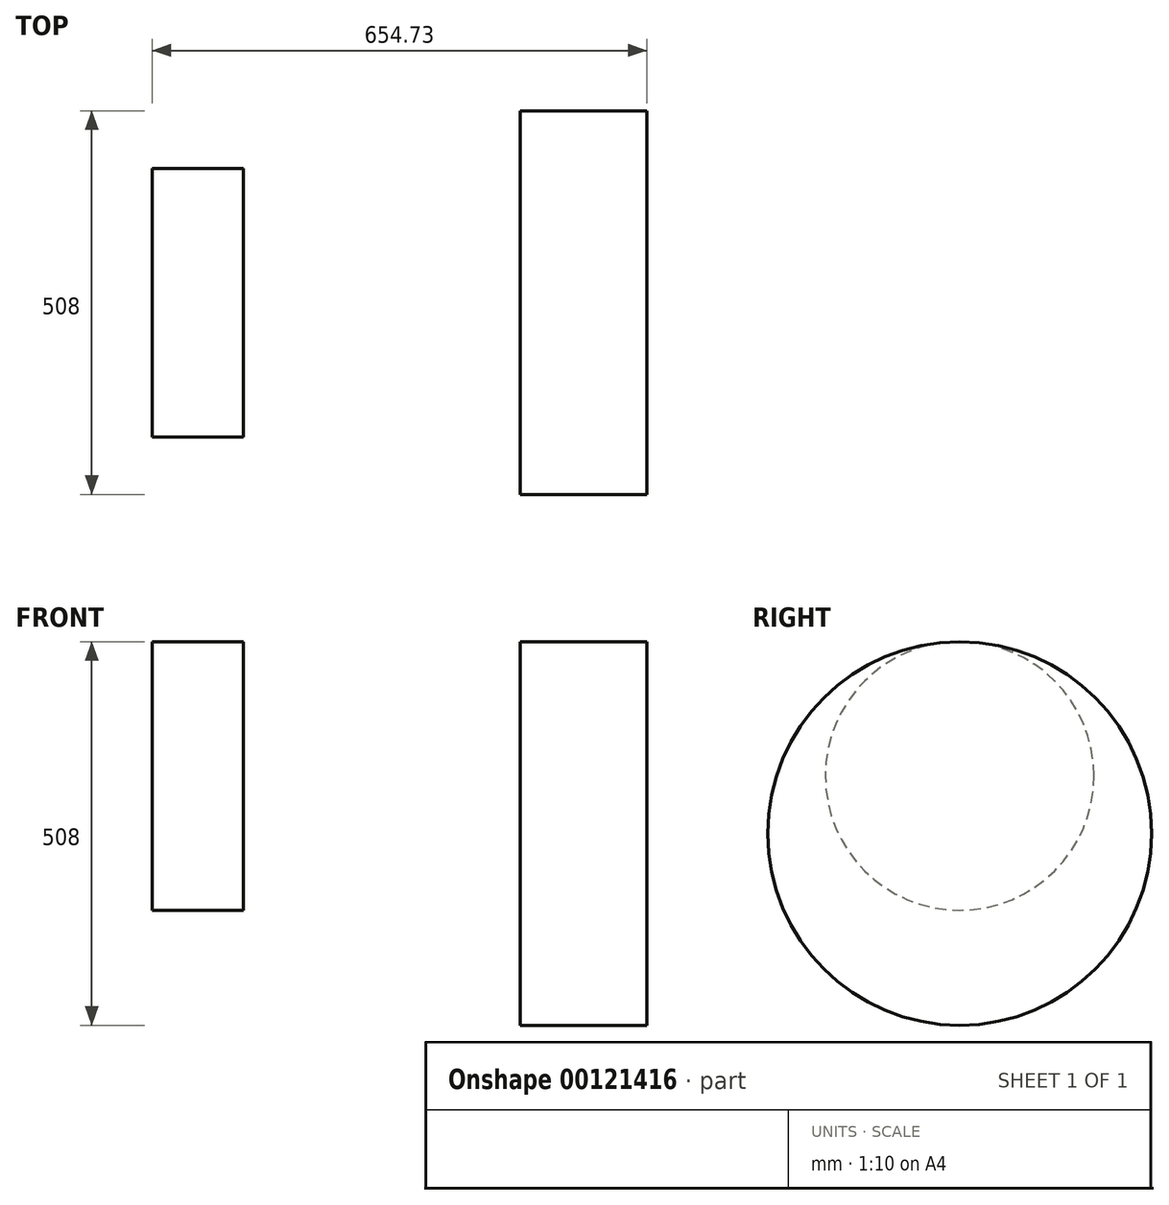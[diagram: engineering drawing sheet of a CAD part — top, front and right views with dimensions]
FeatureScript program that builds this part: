
annotation { "Feature Type Name" : "Feature", "Feature Type Description" : "" }
export const myFeature = defineFeature(function(context is Context, id is Id, definition is map)
    precondition{}
    {
        {
            var Q0;
            Q0=qCreatedBy(makeId("Front.planeOp"),FACE);
            var sketch = newSketch(context, id + "F0", { "sketchPlane" : qUnion([Q0])});
            skLineSegment(sketch, "E0.bottom", {"start": v(-290.57, 177.8) * mm, "end": v(-170, 177.8) * mm});
            skLineSegment(sketch, "E0.top", {"start": v(-290.57, -177.8) * mm, "end": v(-170, -177.8) * mm});
            skLineSegment(sketch, "E0.left", {"start": v(-290.57, 177.8) * mm, "end": v(-290.57, -177.8) * mm});
            skLineSegment(sketch, "E0.right", {"start": v(-170, 177.8) * mm, "end": v(-170, -177.8) * mm});
            skLineSegment(sketch, "E1.bottom", {"start": v(196.28, 177.8) * mm, "end": v(364.16, 177.8) * mm});
            skLineSegment(sketch, "E1.top", {"start": v(196.28, -330.2) * mm, "end": v(364.16, -330.2) * mm});
            skLineSegment(sketch, "E1.left", {"start": v(196.28, 177.8) * mm, "end": v(196.28, -330.2) * mm});
            skLineSegment(sketch, "E1.right", {"start": v(364.16, 177.8) * mm, "end": v(364.16, -330.2) * mm});
            skFitSpline(sketch, "E2", {"points": [v(-170, -177.8) * mm, v(196.28, -330.2) * mm], "startDerivative": vector(816.13, 5.14) * mm, "endDerivative": vector(588.83, 1.78) * mm});
            skLineSegment(sketch, "E3", {"start": v(196.28, -76.2) * mm, "end": v(364.16, -76.2) * mm});
            skLineSegment(sketch, "E4", {"start": v(-290.57, 0) * mm, "end": v(-170, 0) * mm});
            skLineSegment(sketch, "E5", {"start": v(-170, 177.8) * mm, "end": v(196.28, 177.8) * mm});
            skSolve(sketch);
        }
        {
            var Q0;
            {var subQ0=sQuery(id+"F0.wireOp",EDGE,"E1.bottom");Q0=makeQuery(id+"F0.imprint","IMPRINT",FACE,{"disambiguationData":[TD([[makeQuery(id+"F0.imprint","IMPRINT",EDGE,{"derivedFrom":subQ0}),-1.0]])]});}
            var Q1;
            Q1=sQuery(id+"F0.wireOp",EDGE,"E3");
            revolve(context, id + "F1", {"entities" : qUnion([Q0]), "axis" : qUnion([Q1]), "revolveType" : RevolveType.FULL});
        }
        {
            var Q0;
            {var subQ0=sQuery(id+"F0.wireOp",EDGE,"E0.bottom");Q0=makeQuery(id+"F0.imprint","IMPRINT",FACE,{"disambiguationData":[TD([[makeQuery(id+"F0.imprint","IMPRINT",EDGE,{"derivedFrom":subQ0}),-1.0]])]});}
            var Q1;
            Q1=sQuery(id+"F0.wireOp",EDGE,"E4");
            revolve(context, id + "F2", {"entities" : qUnion([Q0]), "axis" : qUnion([Q1]), "revolveType" : RevolveType.FULL});
        }
    });
